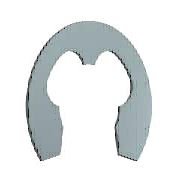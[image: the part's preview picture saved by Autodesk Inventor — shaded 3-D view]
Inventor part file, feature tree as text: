
AUTODESK INVENTOR PART (.ipt)
format: ipt  version: 2014 SP1 (Build 180222100, 222)  size: 159,232 bytes
history: native  units: mm (DEFAULTED — no unit token found)
features: sketch x2, chamfer x2, other x1
ambient origin geometry x8: Origin, YZ Plane, XZ Plane, XY Plane, X Axis, Y Axis, Z Axis, Center Point
bodies: Solid1 (feature_tree)
feature tree (5):
  sketch  "Sketch1"  dims[d0=0.0mm]
  other  "WorkPoint1"
  chamfer  "Chamfer1"  Distance=6.0mm
  chamfer  "Chamfer2"  Distance=5.9mm
  sketch  "Sketch2"  dims[d1=0.0mm d2=6.0mm d3=5.9mm d4=11.5mm d5=11.4mm d6=0.0mm d7=0.0mm d8=9.235294mm d9=9.135294mm d10=1.0mm d11=1.0mm d12=1.0mm d13=1.0mm d14=5.75mm d15=5.7mm d16=5.75mm d17=5.7mm d18=10.0mm d19=9.833333mm d20=1.1mm d21=0.0mm d22=1.418182mm d23=1.14mm d24=1.733333mm d25=1.733333mm d26=1.14mm d28=0.0mm d29=45.0deg d30=45.0deg d32=0.0mm d33=0.0mm d34=0.0mm]
